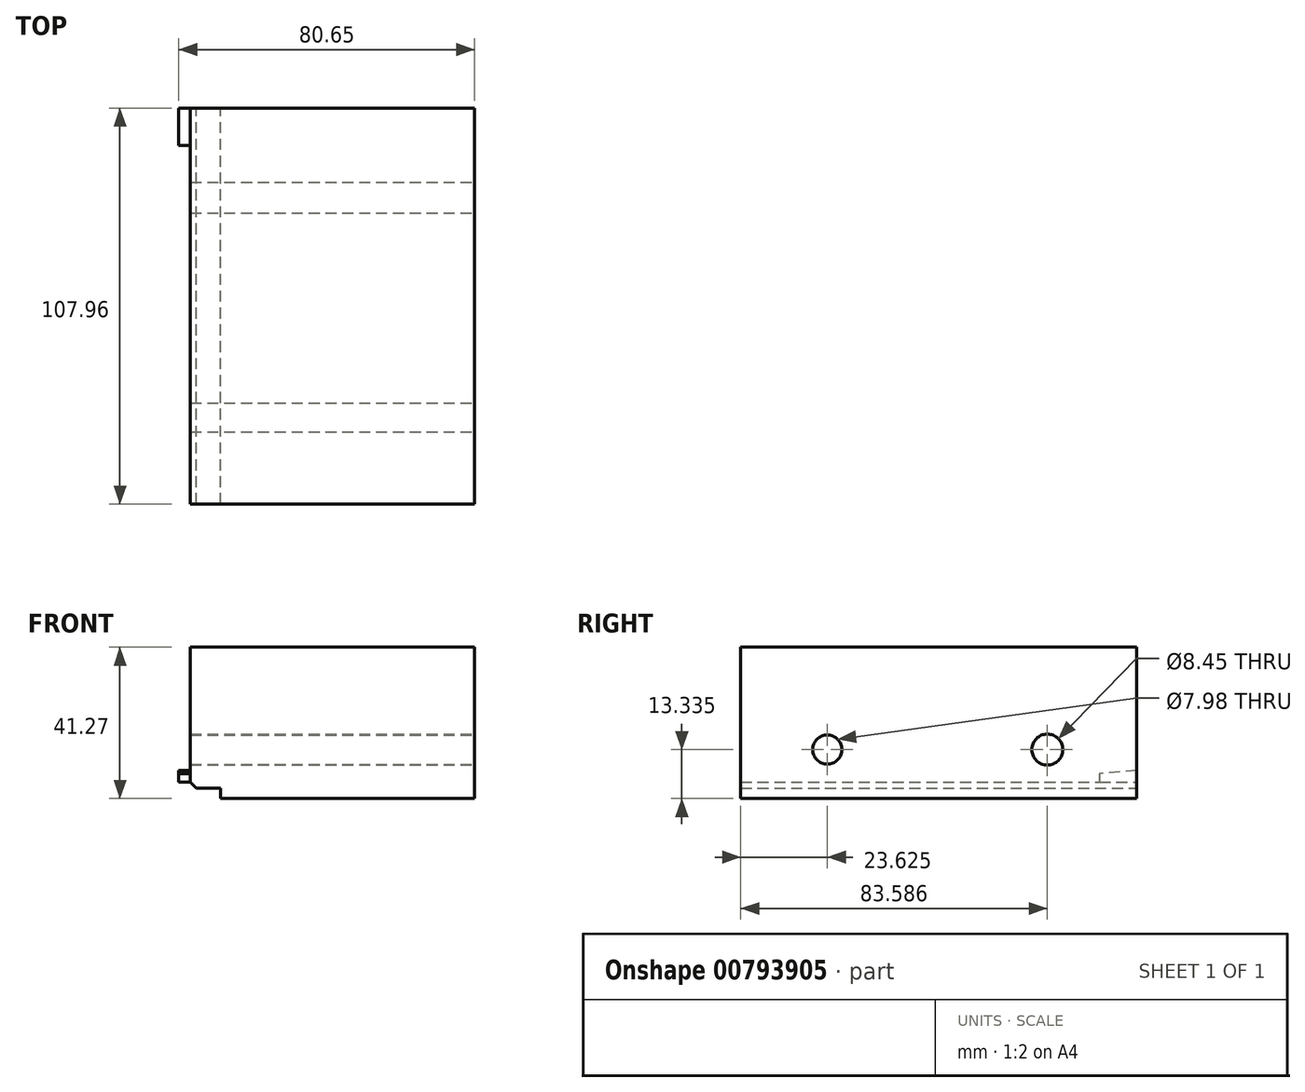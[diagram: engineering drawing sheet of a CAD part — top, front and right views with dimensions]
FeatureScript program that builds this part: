
annotation { "Feature Type Name" : "Feature", "Feature Type Description" : "" }
export const myFeature = defineFeature(function(context is Context, id is Id, definition is map)
    precondition{}
    {
        {
            var Q0;
            Q0=qCreatedBy(makeId("Top.planeOp"),FACE);
            var sketch = newSketch(context, id + "F0", { "sketchPlane" : qUnion([Q0])});
            skLineSegment(sketch, "E0.bottom", {"start": v(38.73, 53.98) * mm, "end": v(-38.74, 53.98) * mm});
            skLineSegment(sketch, "E0.top", {"start": v(38.73, -53.98) * mm, "end": v(-38.73, -53.98) * mm});
            skLineSegment(sketch, "E0.left", {"start": v(38.73, 53.98) * mm, "end": v(38.73, -53.98) * mm});
            skLineSegment(sketch, "E0.right", {"start": v(-38.74, 53.98) * mm, "end": v(-38.73, -53.98) * mm});
            skPoint(sketch, "E0.middle", {"position": v(0, 0) * mm});
            skSolve(sketch);
        }
        {
            var Q0;
            Q0=qSketchRegion(id+"F0",true);
            extrude(context, id + "F1", {"entities" : qUnion([Q0]), "depth" : 41.27 * mm, "offsetDistance" : 25.4 * mm});
        }
        {
            var Q0;
            Q0=makeQuery(id+"F1.opExtrude","SWEPT_FACE",FACE,{"disambiguationData":[OSD([sQuery(id+"F0.wireOp",EDGE,"E0.left")])]});
            var sketch = newSketch(context, id + "F2", { "sketchPlane" : qUnion([Q0])});
            skCircle(sketch, "E1", {"center": v(-30.36, 13.33) * mm, "radius": 3.99 * mm});
            skCircle(sketch, "E2", {"center": v(29.6, 13.33) * mm, "radius": 4.23 * mm});
            skLineSegment(sketch, "E3", {"start": v(67.83, 13.34) * mm, "end": v(-71.4, 13.33) * mm, "construction": true});
            skSolve(sketch);
        }
        {
            var Q0;
            Q0=qSketchRegion(id+"F2",true);
            extrude(context, id + "F3", {"entities" : qUnion([Q0]), "operationType" : NewBodyOperationType.REMOVE, "endBound" : BoundingType.THROUGH_ALL, "oppositeDirection" : true, "depth" : 25.4 * mm, "offsetDistance" : 25.4 * mm});
        }
        {
            var Q0;
            Q0=makeQuery(id+"F1.opExtrude","SWEPT_FACE",FACE,{"disambiguationData":[OSD([sQuery(id+"F0.wireOp",EDGE,"E0.bottom")])]});
            var sketch = newSketch(context, id + "F4", { "sketchPlane" : qUnion([Q0])});
            skLineSegment(sketch, "E4", {"start": v(38.74, 4.45) * mm, "end": v(37.15, 2.86) * mm});
            skLineSegment(sketch, "E5", {"start": v(37.15, 2.86) * mm, "end": v(30.48, 2.86) * mm});
            skLineSegment(sketch, "E6", {"start": v(30.48, 2.86) * mm, "end": v(30.48, 0) * mm});
            skLineSegment(sketch, "E7", {"start": v(30.48, 0) * mm, "end": v(38.74, 0) * mm});
            skLineSegment(sketch, "E8", {"start": v(38.74, 0) * mm, "end": v(38.74, 4.45) * mm});
            skSolve(sketch);
        }
        {
            var Q0;
            Q0=qSketchRegion(id+"F4",true);
            extrude(context, id + "F5", {"entities" : qUnion([Q0]), "operationType" : NewBodyOperationType.REMOVE, "endBound" : BoundingType.THROUGH_ALL, "oppositeDirection" : true, "depth" : 25.4 * mm, "offsetDistance" : 25.4 * mm});
        }
        {
            var Q0;
            Q0=makeQuery(id+"F1.opExtrude","SWEPT_FACE",FACE,{"disambiguationData":[OSD([sQuery(id+"F0.wireOp",EDGE,"E0.right")])]});
            var sketch = newSketch(context, id + "F6", { "sketchPlane" : qUnion([Q0])});
            skLineSegment(sketch, "E9", {"start": v(-53.98, 4.45) * mm, "end": v(-43.82, 4.45) * mm});
            skLineSegment(sketch, "E10", {"start": v(-53.98, 4.45) * mm, "end": v(-53.98, 7.62) * mm});
            skLineSegment(sketch, "E11", {"start": v(-53.98, 7.62) * mm, "end": v(-43.82, 6.73) * mm});
            skLineSegment(sketch, "E12", {"start": v(-43.82, 6.73) * mm, "end": v(-43.82, 4.45) * mm});
            skSolve(sketch);
        }
        {
            var Q0;
            Q0=qSketchRegion(id+"F6",true);
            extrude(context, id + "F7", {"entities" : qUnion([Q0]), "operationType" : NewBodyOperationType.ADD, "depth" : 3.17 * mm, "offsetDistance" : 25.4 * mm});
        }
    });
